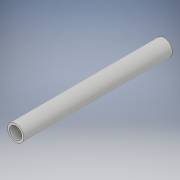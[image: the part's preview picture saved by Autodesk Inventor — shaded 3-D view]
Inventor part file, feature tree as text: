
AUTODESK INVENTOR PART (.ipt)
format: ipt  version: 2018 (Build 220112000, 112)  size: 94,208 bytes
history: native  units: in
note: dims shown in document units (in); Inventor stores cm internally (conversion verified against a paired STEP export)
features: extrude x1, sketch x1
ambient origin geometry x8: Origin, YZ Plane, XZ Plane, XY Plane, X Axis, Y Axis, Z Axis, Center Point
bodies: Solid1 (feature_tree)
feature tree (2):
  extrude  "Extrusion1"  Depth=12.0in
  sketch  "Sketch1"  dims[d0=1.315in d1=1.0in d2=12.0in d3=0.0in]
